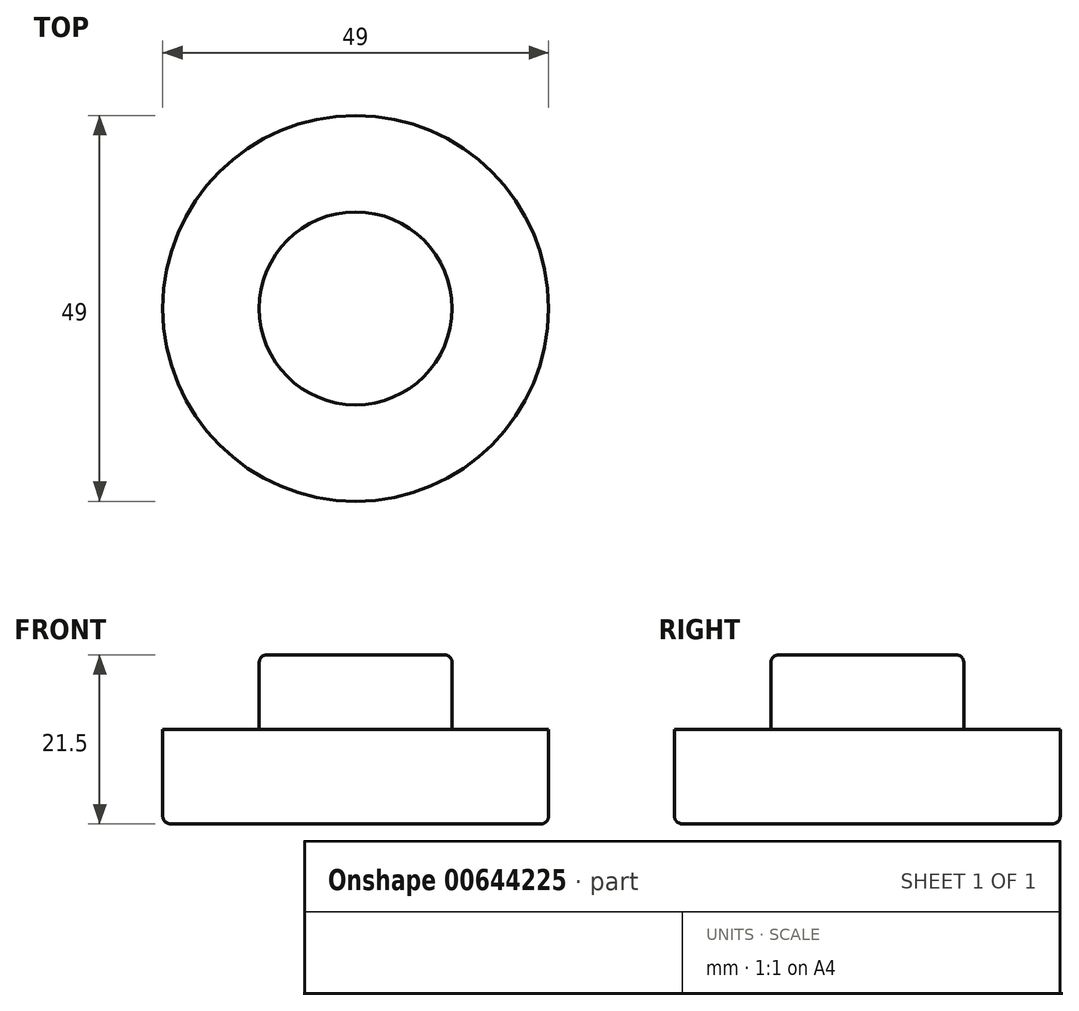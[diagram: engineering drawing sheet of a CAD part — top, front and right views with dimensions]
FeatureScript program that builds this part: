
annotation { "Feature Type Name" : "Feature", "Feature Type Description" : "" }
export const myFeature = defineFeature(function(context is Context, id is Id, definition is map)
    precondition{}
    {
        {
            var Q0;
            Q0=qCreatedBy(makeId("Top.planeOp"),FACE);
            var sketch = newSketch(context, id + "F0", { "sketchPlane" : qUnion([Q0])});
            skCircle(sketch, "E0", {"center": v(0, 0) * mm, "radius": 24.5 * mm});
            skSolve(sketch);
        }
        {
            var Q0;
            Q0=makeQuery(id+"F0.imprint","IMPRINT",FACE,{"disambiguationData":[TD([[makeQuery(id+"F0.imprint","IMPRINT",EDGE,{"derivedFrom":sQuery(id+"F0.wireOp",EDGE,"E0")}),1.0]])]});
            extrude(context, id + "F1", {"entities" : qUnion([Q0]), "depth" : 12 * mm});
        }
        {
            var Q0;
            Q0=makeQuery(id+"F1.opExtrude","CAP_FACE",FACE,{"disambiguationData":[OSD([sQuery(id+"F0.wireOp",EDGE,"E0")])],"isStart":false});
            var sketch = newSketch(context, id + "F2", { "sketchPlane" : qUnion([Q0])});
            skCircle(sketch, "E1", {"center": v(0, 0) * mm, "radius": 12.25 * mm});
            skSolve(sketch);
        }
        {
            var Q0;
            Q0=makeQuery(id+"F2.imprint","IMPRINT",FACE,{"disambiguationData":[TD([[makeQuery(id+"F2.imprint","IMPRINT",EDGE,{"derivedFrom":sQuery(id+"F2.wireOp",EDGE,"E1")}),1.0]])]});
            extrude(context, id + "F3", {"entities" : qUnion([Q0]), "operationType" : NewBodyOperationType.ADD, "depth" : 9.5 * mm});
        }
        {
            var Q0;
            Q0=makeQuery(id+"F3.opExtrude","CAP_EDGE",EDGE,{"disambiguationData":[OSD([sQuery(id+"F2.wireOp",EDGE,"E1")])],"isStart":false});
            var Q1;
            Q1=makeQuery(id+"F1.opExtrude","CAP_EDGE",EDGE,{"disambiguationData":[OSD([sQuery(id+"F0.wireOp",EDGE,"E0")])],"isStart":true});
            fillet(context, id + "F4", {"entities" : qUnion([Q0, Q1]), "radius" : 1 * mm, "tangentPropagation" : true, "allowEdgeOverflow" : false});
        }
    });
